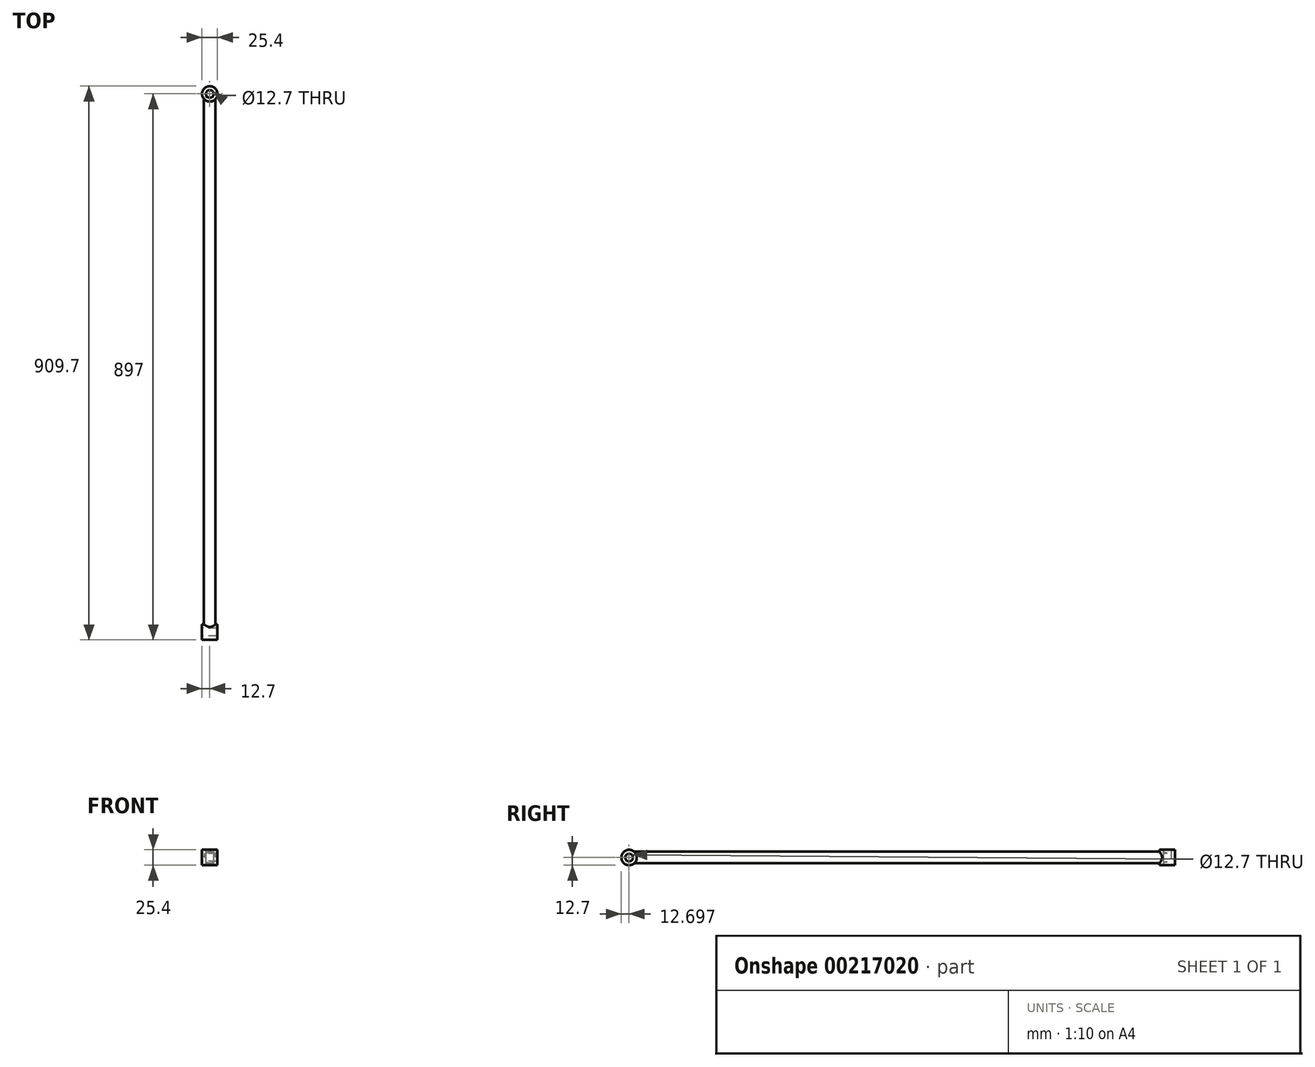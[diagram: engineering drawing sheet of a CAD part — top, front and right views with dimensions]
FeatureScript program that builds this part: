
annotation { "Feature Type Name" : "Feature", "Feature Type Description" : "" }
export const myFeature = defineFeature(function(context is Context, id is Id, definition is map)
    precondition{}
    {
        {
            var Q0;
            Q0=qCreatedBy(makeId("Top.planeOp"),FACE);
            var sketch = newSketch(context, id + "F0", { "sketchPlane" : qUnion([Q0])});
            skCircle(sketch, "E0", {"center": v(0, 0) * mm, "radius": 12.7 * mm});
            skCircle(sketch, "E1", {"center": v(0, 0) * mm, "radius": 6.35 * mm});
            skSolve(sketch);
        }
        {
            var Q0;
            Q0=qCreatedBy(makeId("Front.planeOp"),FACE);
            var sketch = newSketch(context, id + "F1", { "sketchPlane" : qUnion([Q0])});
            skCircle(sketch, "E2", {"center": v(0, 0) * mm, "radius": 9.53 * mm});
            skSolve(sketch);
        }
        {
            var Q0;
            Q0 = qSketchRegion(id + "F1", true);
            extrude(context, id + "F2", {"entities" : qUnion([Q0]), "depth" : 876.3 * mm});
        }
        {
            var Q0;
            Q0=makeQuery(id+"F0.imprint","IMPRINT",FACE,{"disambiguationData":[TD([[makeQuery(id+"F0.imprint","IMPRINT",EDGE,{"derivedFrom":sQuery(id+"F0.wireOp",EDGE,"E0")}),1.0]])]});
            extrude(context, id + "F3", {"entities" : qUnion([Q0]), "operationType" : NewBodyOperationType.ADD, "depth" : 25.4 * mm, "symmetric" : true});
        }
        {
            var Q0;
            Q0=makeQuery(id+"F2.opExtrude","CAP_FACE",FACE,{"disambiguationData":[OSD([sQuery(id+"F1.wireOp",EDGE,"E2")])],"isStart":true});
            var Q1;
            Q1=makeQuery(id+"F3.opExtrude","SWEPT_FACE",FACE,{"disambiguationData":[OSD([sQuery(id+"F0.wireOp",EDGE,"E0")])]});
            extrude(context, id + "F4", {"entities" : qUnion([Q0]), "operationType" : NewBodyOperationType.REMOVE, "oppositeDirection" : true, "endBoundEntityFace" : qUnion([Q1]), "depth" : 6.35 * mm});
        }
        {
            var Q0;
            Q0=qCreatedBy(makeId("Right.planeOp"),FACE);
            var sketch = newSketch(context, id + "F5", { "sketchPlane" : qUnion([Q0])});
            skCircle(sketch, "E3", {"center": v(-884.3, 0) * mm, "radius": 12.7 * mm});
            skCircle(sketch, "E4", {"center": v(-884.3, 0) * mm, "radius": 6.35 * mm});
            skSolve(sketch);
        }
        {
            var Q0;
            Q0=makeQuery(id+"F5.imprint","IMPRINT",FACE,{"disambiguationData":[TD([[makeQuery(id+"F5.imprint","IMPRINT",EDGE,{"derivedFrom":sQuery(id+"F5.wireOp",EDGE,"E3")}),1.0]])]});
            extrude(context, id + "F6", {"entities" : qUnion([Q0]), "operationType" : NewBodyOperationType.ADD, "depth" : 25.4 * mm, "symmetric" : true});
        }
    });
